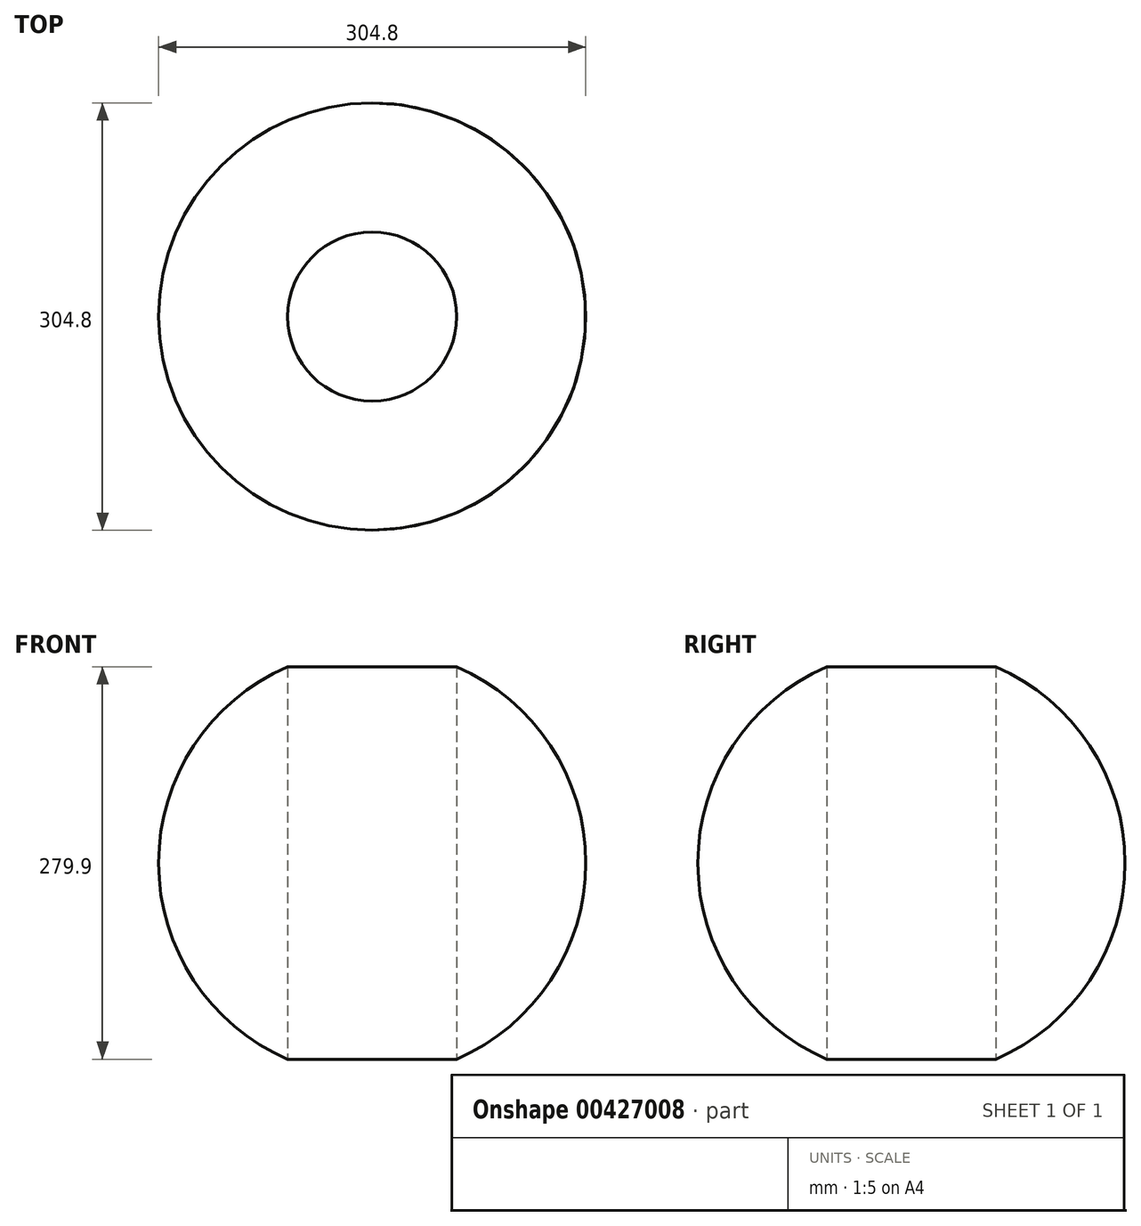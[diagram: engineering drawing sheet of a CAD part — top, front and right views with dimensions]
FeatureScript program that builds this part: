
annotation { "Feature Type Name" : "Feature", "Feature Type Description" : "" }
export const myFeature = defineFeature(function(context is Context, id is Id, definition is map)
    precondition{}
    {
        {
            var Q0;
            Q0=qCreatedBy(makeId("Top.planeOp"),FACE);
            var sketch = newSketch(context, id + "F0", { "sketchPlane" : qUnion([Q0])});
            skCircle(sketch, "E0", {"center": v(0, 0) * mm, "radius": 60.33 * mm});
            skSolve(sketch);
        }
        {
            var Q0;
            Q0=qCreatedBy(makeId("Top.planeOp"),FACE);
            var sketch = newSketch(context, id + "F1", { "sketchPlane" : qUnion([Q0])});
            skArc(sketch, "E1", {"start": v(0, 152.4) * mm, "mid": v(-152.4, 0) * mm, "end": v(0, -152.4) * mm});
            skLineSegment(sketch, "E2", {"start": v(0, 0) * mm, "end": v(0, 192.24) * mm, "construction": true});
            skLineSegment(sketch, "E3", {"start": v(0, 0) * mm, "end": v(0, -321.28) * mm, "construction": true});
            skLineSegment(sketch, "E4", {"start": v(0, -152.4) * mm, "end": v(0, 152.4) * mm});
            skSolve(sketch);
        }
        {
            var Q0;
            Q0 = qSketchRegion(id + "F1", true);
            var Q1;
            Q1=sQuery(id+"F1.wireOp",EDGE,"E2");
            revolve(context, id + "F2", {"entities" : qUnion([Q0]), "axis" : qUnion([Q1]), "revolveType" : RevolveType.FULL});
        }
        {
            var Q0;
            Q0 = qSketchRegion(id + "F0", true);
            extrude(context, id + "F3", {"entities" : qUnion([Q0]), "operationType" : NewBodyOperationType.REMOVE, "endBound" : BoundingType.THROUGH_ALL, "depth" : 25.4 * mm, "hasSecondDirection" : true, "secondDirectionBound" : SecondDirectionBoundingType.THROUGH_ALL, "secondDirectionOppositeDirection" : true, "secondDirectionDepth" : 25.4 * mm});
        }
    });
